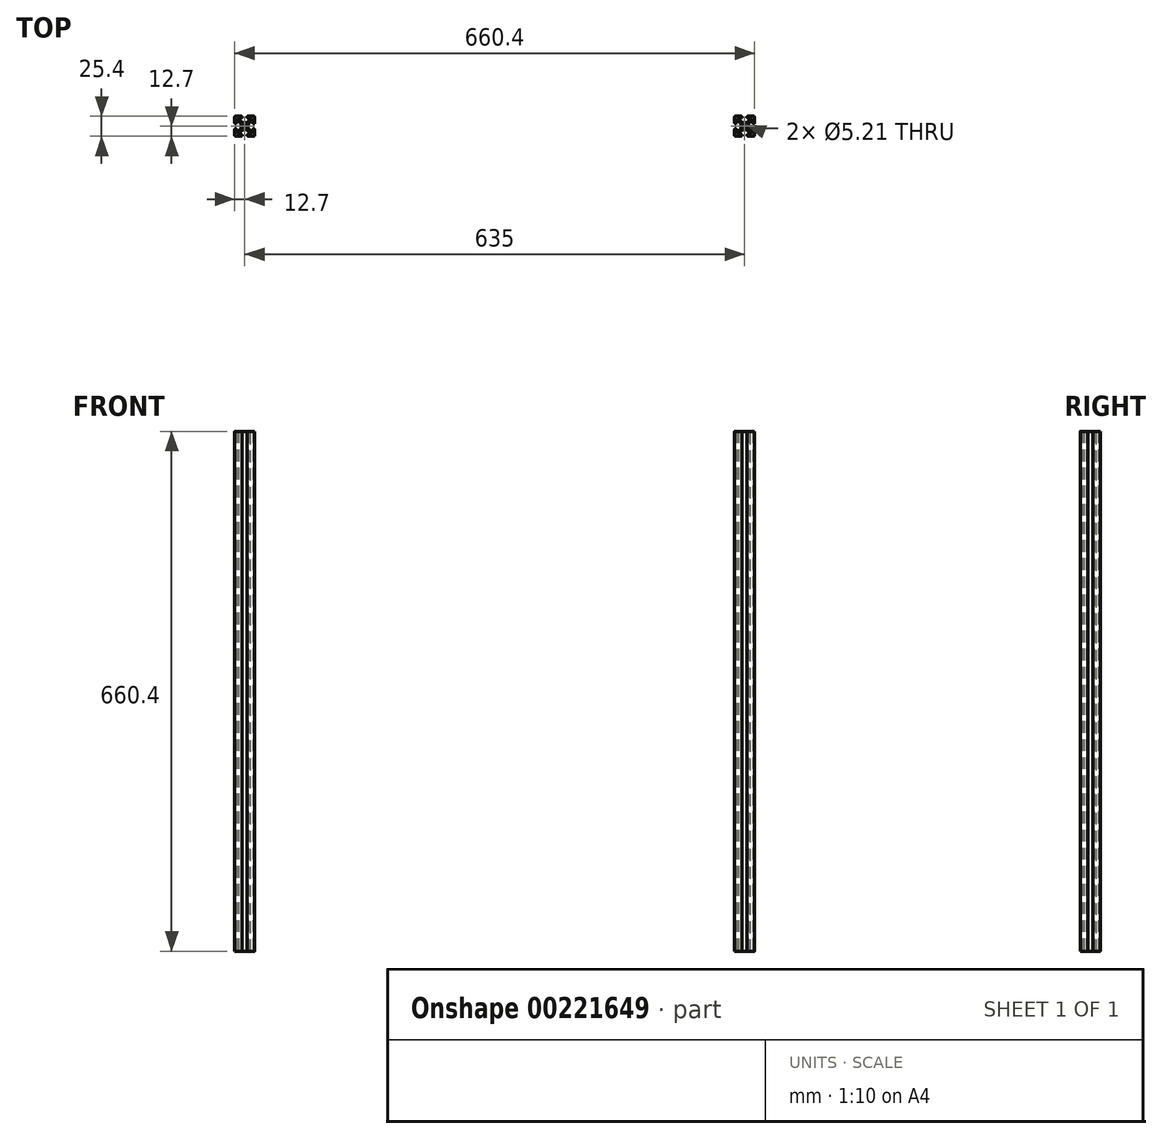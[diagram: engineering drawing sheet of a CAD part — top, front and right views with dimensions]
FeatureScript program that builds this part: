
annotation { "Feature Type Name" : "Feature", "Feature Type Description" : "" }
export const myFeature = defineFeature(function(context is Context, id is Id, definition is map)
    precondition{}
    {
        {
            var Q0;
            Q0=qCreatedBy(makeId("Top.planeOp"),FACE);
            var sketch = newSketch(context, id + "F0", { "sketchPlane" : qUnion([Q0])});
            skLineSegment(sketch, "E0.bottom", {"start": v(12.7, 12.7) * mm, "end": v(-12.7, 12.7) * mm});
            skLineSegment(sketch, "E0.top", {"start": v(12.7, -12.7) * mm, "end": v(-12.7, -12.7) * mm});
            skLineSegment(sketch, "E0.left", {"start": v(12.7, 12.7) * mm, "end": v(12.7, -12.7) * mm});
            skLineSegment(sketch, "E0.right", {"start": v(-12.7, 12.7) * mm, "end": v(-12.7, -12.7) * mm});
            skPoint(sketch, "E0.middle", {"position": v(0, 0) * mm});
            skCircle(sketch, "E1", {"center": v(0, 0) * mm, "radius": 2.6 * mm});
            skLineSegment(sketch, "E2", {"start": v(-12.7, 12.7) * mm, "end": v(12.7, -12.7) * mm, "construction": true});
            skLineSegment(sketch, "E3", {"start": v(0, 12.7) * mm, "end": v(0, -12.7) * mm, "construction": true});
            skLineSegment(sketch, "E4", {"start": v(-12.7, -12.7) * mm, "end": v(12.7, 12.7) * mm, "construction": true});
            skLineSegment(sketch, "E5", {"start": v(-8.78, 10.34) * mm, "end": v(-2.95, 4.5) * mm});
            skLineSegment(sketch, "E6.MirrorCS", {"start": v(8.78, 10.34) * mm, "end": v(2.95, 4.5) * mm});
            skLineSegment(sketch, "E7", {"start": v(-2.95, 4.5) * mm, "end": v(2.95, 4.5) * mm});
            skLineSegment(sketch, "E8.bottom", {"start": v(-3.24, 14.9) * mm, "end": v(3.24, 14.9) * mm});
            skLineSegment(sketch, "E8.left", {"start": v(-3.24, 14.9) * mm, "end": v(-3.24, 10.34) * mm});
            skLineSegment(sketch, "E8.right", {"start": v(3.24, 14.9) * mm, "end": v(3.24, 10.34) * mm});
            skLineSegment(sketch, "E9", {"start": v(-8.78, 10.34) * mm, "end": v(-3.24, 10.34) * mm});
            skLineSegment(sketch, "E10", {"start": v(3.24, 10.34) * mm, "end": v(8.78, 10.34) * mm});
            skLineSegment(sketch, "E11.MirrorCS", {"start": v(-10.34, 8.78) * mm, "end": v(-4.5, 2.95) * mm});
            skLineSegment(sketch, "E12.MirrorCS", {"start": v(-10.34, 8.78) * mm, "end": v(-10.34, 3.24) * mm});
            skLineSegment(sketch, "E13.MirrorCS", {"start": v(-14.9, 3.24) * mm, "end": v(-10.34, 3.24) * mm});
            skLineSegment(sketch, "E14.MirrorCS", {"start": v(-14.9, 3.24) * mm, "end": v(-14.9, -3.24) * mm});
            skLineSegment(sketch, "E15.MirrorCS", {"start": v(-14.9, -3.24) * mm, "end": v(-10.34, -3.24) * mm});
            skLineSegment(sketch, "E16.MirrorCS", {"start": v(-10.34, -3.24) * mm, "end": v(-10.34, -8.78) * mm});
            skLineSegment(sketch, "E17.MirrorCS", {"start": v(-10.34, -8.78) * mm, "end": v(-4.5, -2.95) * mm});
            skLineSegment(sketch, "E18.MirrorCS", {"start": v(-4.5, 2.95) * mm, "end": v(-4.5, -2.95) * mm});
            skLineSegment(sketch, "E19.MirrorCS", {"start": v(10.34, 8.78) * mm, "end": v(4.5, 2.95) * mm});
            skLineSegment(sketch, "E20.MirrorCS", {"start": v(4.5, -2.95) * mm, "end": v(4.5, 2.95) * mm});
            skLineSegment(sketch, "E21.MirrorCS", {"start": v(10.34, -8.78) * mm, "end": v(4.5, -2.95) * mm});
            skLineSegment(sketch, "E22.MirrorCS", {"start": v(10.34, -8.78) * mm, "end": v(10.34, -3.24) * mm});
            skLineSegment(sketch, "E23.MirrorCS", {"start": v(14.9, -3.24) * mm, "end": v(10.34, -3.24) * mm});
            skLineSegment(sketch, "E24.MirrorCS", {"start": v(14.9, -3.24) * mm, "end": v(14.9, 3.24) * mm});
            skLineSegment(sketch, "E25.MirrorCS", {"start": v(14.9, 3.24) * mm, "end": v(10.34, 3.24) * mm});
            skLineSegment(sketch, "E26.MirrorCS", {"start": v(10.34, 3.24) * mm, "end": v(10.34, 8.78) * mm});
            skLineSegment(sketch, "E27", {"start": v(-12.7, 0) * mm, "end": v(12.7, 0) * mm, "construction": true});
            skLineSegment(sketch, "E28.MirrorCS", {"start": v(-8.78, -10.34) * mm, "end": v(-2.95, -4.5) * mm});
            skLineSegment(sketch, "E29.MirrorCS", {"start": v(-8.78, -10.34) * mm, "end": v(-3.24, -10.34) * mm});
            skLineSegment(sketch, "E30.MirrorCS", {"start": v(-3.24, -14.9) * mm, "end": v(-3.24, -10.34) * mm});
            skLineSegment(sketch, "E31.MirrorCS", {"start": v(-3.24, -14.9) * mm, "end": v(3.24, -14.9) * mm});
            skLineSegment(sketch, "E32.MirrorCS", {"start": v(3.24, -14.9) * mm, "end": v(3.24, -10.34) * mm});
            skLineSegment(sketch, "E33.MirrorCS", {"start": v(3.24, -10.34) * mm, "end": v(8.78, -10.34) * mm});
            skLineSegment(sketch, "E34.MirrorCS", {"start": v(8.78, -10.34) * mm, "end": v(2.95, -4.5) * mm});
            skLineSegment(sketch, "E35.MirrorCS", {"start": v(-2.95, -4.5) * mm, "end": v(2.95, -4.5) * mm});
            skSolve(sketch);
        }
        {
            var Q0;
            Q0=makeQuery(id+"F0.imprint","IMPRINT",FACE,{"disambiguationData":[TD([[makeQuery(id+"F0.imprint","IMPRINT",EDGE,{"derivedFrom":sQuery(id+"F0.wireOp",EDGE,"E1")}),-1.0]])]});
            extrude(context, id + "F1", {"entities" : qUnion([Q0]), "depth" : 660.4 * mm});
        }
        {
            var Q0;
            Q0=makeQuery(id+"F1.opExtrude","SWEPT_EDGE",EDGE,{"disambiguationData":[OSD([sQuery(id+"F0.wireOp",EDGE,"E0.bottom"),sQuery(id+"F0.wireOp",EDGE,"E8.right")])]});
            var Q1;
            Q1=makeQuery(id+"F1.opExtrude","SWEPT_EDGE",EDGE,{"disambiguationData":[OSD([sQuery(id+"F0.wireOp",EDGE,"E8.right"),sQuery(id+"F0.wireOp",EDGE,"E10")])]});
            var Q2;
            Q2=makeQuery(id+"F1.opExtrude","SWEPT_EDGE",EDGE,{"disambiguationData":[OSD([sQuery(id+"F0.wireOp",EDGE,"E0.bottom"),sQuery(id+"F0.wireOp",EDGE,"E8.left")])]});
            var Q3;
            Q3=makeQuery(id+"F1.opExtrude","SWEPT_EDGE",EDGE,{"disambiguationData":[OSD([sQuery(id+"F0.wireOp",EDGE,"E0.right"),sQuery(id+"F0.wireOp",EDGE,"E13.MirrorCS")])]});
            var Q4;
            Q4=makeQuery(id+"F1.opExtrude","SWEPT_EDGE",EDGE,{"disambiguationData":[OSD([sQuery(id+"F0.wireOp",EDGE,"E8.left"),sQuery(id+"F0.wireOp",EDGE,"E9")])]});
            var Q5;
            Q5=makeQuery(id+"F1.opExtrude","SWEPT_EDGE",EDGE,{"disambiguationData":[OSD([sQuery(id+"F0.wireOp",EDGE,"E12.MirrorCS"),sQuery(id+"F0.wireOp",EDGE,"E13.MirrorCS")])]});
            var Q6;
            Q6=makeQuery(id+"F1.opExtrude","SWEPT_EDGE",EDGE,{"disambiguationData":[OSD([sQuery(id+"F0.wireOp",EDGE,"E0.left"),sQuery(id+"F0.wireOp",EDGE,"E25.MirrorCS")])]});
            var Q7;
            Q7=makeQuery(id+"F1.opExtrude","SWEPT_EDGE",EDGE,{"disambiguationData":[OSD([sQuery(id+"F0.wireOp",EDGE,"E25.MirrorCS"),sQuery(id+"F0.wireOp",EDGE,"E26.MirrorCS")])]});
            var Q8;
            Q8=makeQuery(id+"F1.opExtrude","SWEPT_EDGE",EDGE,{"disambiguationData":[OSD([sQuery(id+"F0.wireOp",EDGE,"E0.left"),sQuery(id+"F0.wireOp",EDGE,"E23.MirrorCS")])]});
            var Q9;
            Q9=makeQuery(id+"F1.opExtrude","SWEPT_EDGE",EDGE,{"disambiguationData":[OSD([sQuery(id+"F0.wireOp",EDGE,"E22.MirrorCS"),sQuery(id+"F0.wireOp",EDGE,"E23.MirrorCS")])]});
            var Q10;
            Q10=makeQuery(id+"F1.opExtrude","SWEPT_EDGE",EDGE,{"disambiguationData":[OSD([sQuery(id+"F0.wireOp",EDGE,"E32.MirrorCS"),sQuery(id+"F0.wireOp",EDGE,"E33.MirrorCS")])]});
            var Q11;
            Q11=makeQuery(id+"F1.opExtrude","SWEPT_EDGE",EDGE,{"disambiguationData":[OSD([sQuery(id+"F0.wireOp",EDGE,"E29.MirrorCS"),sQuery(id+"F0.wireOp",EDGE,"E30.MirrorCS")])]});
            var Q12;
            Q12=makeQuery(id+"F1.opExtrude","SWEPT_EDGE",EDGE,{"disambiguationData":[OSD([sQuery(id+"F0.wireOp",EDGE,"E15.MirrorCS"),sQuery(id+"F0.wireOp",EDGE,"E16.MirrorCS")])]});
            var Q13;
            Q13=makeQuery(id+"F1.opExtrude","SWEPT_EDGE",EDGE,{"disambiguationData":[OSD([sQuery(id+"F0.wireOp",EDGE,"E0.right"),sQuery(id+"F0.wireOp",EDGE,"E15.MirrorCS")])]});
            var Q14;
            Q14=makeQuery(id+"F1.opExtrude","SWEPT_EDGE",EDGE,{"disambiguationData":[OSD([sQuery(id+"F0.wireOp",EDGE,"E0.top"),sQuery(id+"F0.wireOp",EDGE,"E30.MirrorCS")])]});
            var Q15;
            Q15=makeQuery(id+"F1.opExtrude","SWEPT_EDGE",EDGE,{"disambiguationData":[OSD([sQuery(id+"F0.wireOp",EDGE,"E0.top"),sQuery(id+"F0.wireOp",EDGE,"E32.MirrorCS")])]});
            fillet(context, id + "F2", {"entities" : qUnion([Q0, Q1, Q2, Q3, Q4, Q5, Q6, Q7, Q8, Q9, Q10, Q11, Q12, Q13, Q14, Q15]), "radius" : 1.18 * mm, "tangentPropagation" : true, "allowEdgeOverflow" : false});
        }
        {
            var Q0;
            Q0=makeQuery(id+"F1.opExtrude","SWEPT_EDGE",EDGE,{"disambiguationData":[OSD([sQuery(id+"F0.wireOp",EDGE,"E6.MirrorCS"),sQuery(id+"F0.wireOp",EDGE,"E7")])]});
            var Q1;
            Q1=makeQuery(id+"F1.opExtrude","SWEPT_EDGE",EDGE,{"disambiguationData":[OSD([sQuery(id+"F0.wireOp",EDGE,"E5"),sQuery(id+"F0.wireOp",EDGE,"E7")])]});
            var Q2;
            Q2=makeQuery(id+"F1.opExtrude","SWEPT_EDGE",EDGE,{"disambiguationData":[OSD([sQuery(id+"F0.wireOp",EDGE,"E20.MirrorCS"),sQuery(id+"F0.wireOp",EDGE,"E21.MirrorCS")])]});
            var Q3;
            Q3=makeQuery(id+"F1.opExtrude","SWEPT_EDGE",EDGE,{"disambiguationData":[OSD([sQuery(id+"F0.wireOp",EDGE,"E19.MirrorCS"),sQuery(id+"F0.wireOp",EDGE,"E20.MirrorCS")])]});
            var Q4;
            Q4=makeQuery(id+"F1.opExtrude","SWEPT_EDGE",EDGE,{"disambiguationData":[OSD([sQuery(id+"F0.wireOp",EDGE,"E34.MirrorCS"),sQuery(id+"F0.wireOp",EDGE,"E35.MirrorCS")])]});
            var Q5;
            Q5=makeQuery(id+"F1.opExtrude","SWEPT_EDGE",EDGE,{"disambiguationData":[OSD([sQuery(id+"F0.wireOp",EDGE,"E28.MirrorCS"),sQuery(id+"F0.wireOp",EDGE,"E35.MirrorCS")])]});
            var Q6;
            Q6=makeQuery(id+"F1.opExtrude","SWEPT_EDGE",EDGE,{"disambiguationData":[OSD([sQuery(id+"F0.wireOp",EDGE,"E17.MirrorCS"),sQuery(id+"F0.wireOp",EDGE,"E18.MirrorCS")])]});
            var Q7;
            Q7=makeQuery(id+"F1.opExtrude","SWEPT_EDGE",EDGE,{"disambiguationData":[OSD([sQuery(id+"F0.wireOp",EDGE,"E11.MirrorCS"),sQuery(id+"F0.wireOp",EDGE,"E18.MirrorCS")])]});
            fillet(context, id + "F3", {"entities" : qUnion([Q0, Q1, Q2, Q3, Q4, Q5, Q6, Q7]), "radius" : 5.08 * mm, "tangentPropagation" : true, "allowEdgeOverflow" : false});
        }
        {
            var Q0;
            Q0=makeQuery(id+"F1.opExtrude","SWEPT_EDGE",EDGE,{"disambiguationData":[OSD([sQuery(id+"F0.wireOp",EDGE,"E6.MirrorCS"),sQuery(id+"F0.wireOp",EDGE,"E10")])]});
            var Q1;
            Q1=makeQuery(id+"F1.opExtrude","SWEPT_EDGE",EDGE,{"disambiguationData":[OSD([sQuery(id+"F0.wireOp",EDGE,"E5"),sQuery(id+"F0.wireOp",EDGE,"E9")])]});
            var Q2;
            Q2=makeQuery(id+"F1.opExtrude","SWEPT_EDGE",EDGE,{"disambiguationData":[OSD([sQuery(id+"F0.wireOp",EDGE,"E11.MirrorCS"),sQuery(id+"F0.wireOp",EDGE,"E12.MirrorCS")])]});
            var Q3;
            Q3=makeQuery(id+"F1.opExtrude","SWEPT_EDGE",EDGE,{"disambiguationData":[OSD([sQuery(id+"F0.wireOp",EDGE,"E16.MirrorCS"),sQuery(id+"F0.wireOp",EDGE,"E17.MirrorCS")])]});
            var Q4;
            Q4=makeQuery(id+"F1.opExtrude","SWEPT_EDGE",EDGE,{"disambiguationData":[OSD([sQuery(id+"F0.wireOp",EDGE,"E28.MirrorCS"),sQuery(id+"F0.wireOp",EDGE,"E29.MirrorCS")])]});
            var Q5;
            Q5=makeQuery(id+"F1.opExtrude","SWEPT_EDGE",EDGE,{"disambiguationData":[OSD([sQuery(id+"F0.wireOp",EDGE,"E33.MirrorCS"),sQuery(id+"F0.wireOp",EDGE,"E34.MirrorCS")])]});
            var Q6;
            Q6=makeQuery(id+"F1.opExtrude","SWEPT_EDGE",EDGE,{"disambiguationData":[OSD([sQuery(id+"F0.wireOp",EDGE,"E21.MirrorCS"),sQuery(id+"F0.wireOp",EDGE,"E22.MirrorCS")])]});
            var Q7;
            Q7=makeQuery(id+"F1.opExtrude","SWEPT_EDGE",EDGE,{"disambiguationData":[OSD([sQuery(id+"F0.wireOp",EDGE,"E19.MirrorCS"),sQuery(id+"F0.wireOp",EDGE,"E26.MirrorCS")])]});
            fillet(context, id + "F4", {"entities" : qUnion([Q0, Q1, Q2, Q3, Q4, Q5, Q6, Q7]), "radius" : 0.76 * mm, "tangentPropagation" : true, "allowEdgeOverflow" : false});
        }
        {
            var Q0;
            Q0=makeQuery(id+"F1.opExtrude","SWEPT_EDGE",EDGE,{"disambiguationData":[OSD([sQuery(id+"F0.wireOp",EDGE,"E0.top"),sQuery(id+"F0.wireOp",EDGE,"E0.right")])]});
            var Q1;
            Q1=makeQuery(id+"F1.opExtrude","SWEPT_EDGE",EDGE,{"disambiguationData":[OSD([sQuery(id+"F0.wireOp",EDGE,"E0.top"),sQuery(id+"F0.wireOp",EDGE,"E0.left")])]});
            var Q2;
            Q2=makeQuery(id+"F1.opExtrude","SWEPT_EDGE",EDGE,{"disambiguationData":[OSD([sQuery(id+"F0.wireOp",EDGE,"E0.bottom"),sQuery(id+"F0.wireOp",EDGE,"E0.left")])]});
            var Q3;
            Q3=makeQuery(id+"F1.opExtrude","SWEPT_EDGE",EDGE,{"disambiguationData":[OSD([sQuery(id+"F0.wireOp",EDGE,"E0.bottom"),sQuery(id+"F0.wireOp",EDGE,"E0.right")])]});
            fillet(context, id + "F5", {"entities" : qUnion([Q0, Q1, Q2, Q3]), "radius" : 1.27 * mm, "tangentPropagation" : true, "allowEdgeOverflow" : false});
        }
        {
            var Q0;
            Q0=makeQuery(id+"F1.opExtrude","SWEPT_BODY",BODY,{"disambiguationData":[OSD([sQuery(id+"F0.wireOp",EDGE,"E0.bottom"),sQuery(id+"F0.wireOp",EDGE,"E0.top"),sQuery(id+"F0.wireOp",EDGE,"E0.left"),sQuery(id+"F0.wireOp",EDGE,"E0.right"),sQuery(id+"F0.wireOp",EDGE,"E1"),sQuery(id+"F0.wireOp",EDGE,"E5"),sQuery(id+"F0.wireOp",EDGE,"E6.MirrorCS"),sQuery(id+"F0.wireOp",EDGE,"E7"),sQuery(id+"F0.wireOp",EDGE,"E8.left"),sQuery(id+"F0.wireOp",EDGE,"E8.right"),sQuery(id+"F0.wireOp",EDGE,"E9"),sQuery(id+"F0.wireOp",EDGE,"E10"),sQuery(id+"F0.wireOp",EDGE,"E11.MirrorCS"),sQuery(id+"F0.wireOp",EDGE,"E12.MirrorCS"),sQuery(id+"F0.wireOp",EDGE,"E13.MirrorCS"),sQuery(id+"F0.wireOp",EDGE,"E15.MirrorCS"),sQuery(id+"F0.wireOp",EDGE,"E16.MirrorCS"),sQuery(id+"F0.wireOp",EDGE,"E17.MirrorCS"),sQuery(id+"F0.wireOp",EDGE,"E18.MirrorCS"),sQuery(id+"F0.wireOp",EDGE,"E19.MirrorCS"),sQuery(id+"F0.wireOp",EDGE,"E20.MirrorCS"),sQuery(id+"F0.wireOp",EDGE,"E21.MirrorCS"),sQuery(id+"F0.wireOp",EDGE,"E22.MirrorCS"),sQuery(id+"F0.wireOp",EDGE,"E23.MirrorCS"),sQuery(id+"F0.wireOp",EDGE,"E25.MirrorCS"),sQuery(id+"F0.wireOp",EDGE,"E26.MirrorCS"),sQuery(id+"F0.wireOp",EDGE,"E28.MirrorCS"),sQuery(id+"F0.wireOp",EDGE,"E29.MirrorCS"),sQuery(id+"F0.wireOp",EDGE,"E30.MirrorCS"),sQuery(id+"F0.wireOp",EDGE,"E32.MirrorCS"),sQuery(id+"F0.wireOp",EDGE,"E33.MirrorCS"),sQuery(id+"F0.wireOp",EDGE,"E34.MirrorCS"),sQuery(id+"F0.wireOp",EDGE,"E35.MirrorCS")])]});
            var Q1;
            {var subQ0=sQuery(id+"F0.wireOp",EDGE,"E0.left");Q1=makeQuery(id+"F1.opExtrude","SWEPT_FACE",FACE,{"disambiguationData":[OSD([subQ0]),TDD([makeQuery(id+"F0.imprint","IMPRINT",EDGE,{"disambiguationData":[TD([[makeQuery(id+"F0.imprint","INTERSECT",VERTEX,{"derivedFrom":[sQuery(id+"F0.wireOp",EDGE,"E0.bottom"),subQ0]}),-1.0]])],"derivedFrom":subQ0})])]});}
            transform(context, id + "F6", {"entities" : qUnion([Q0]), "transformType" : TransformType.TRANSLATION_3D, "dx" : 635 * mm, "dy" : 0 * mm, "dz" : 0 * mm, "makeCopy" : true});
        }
    });
